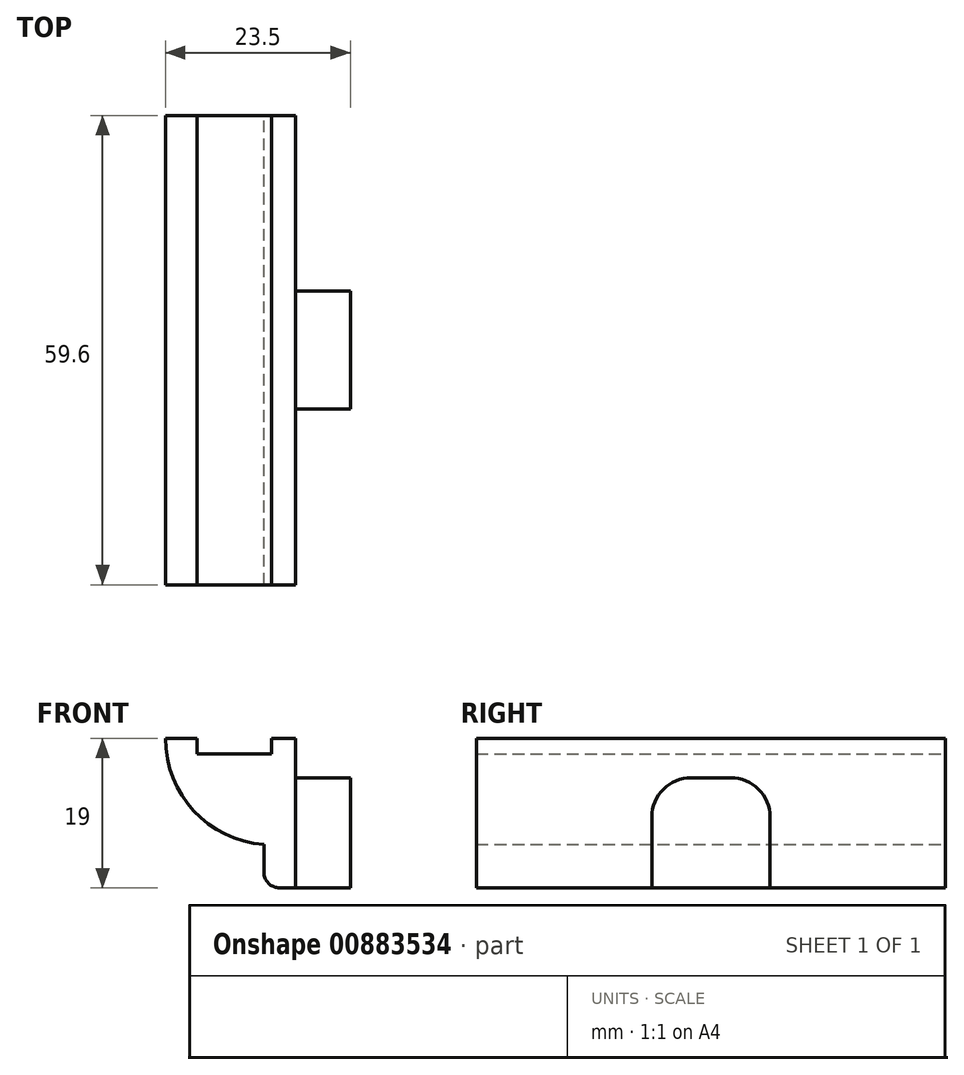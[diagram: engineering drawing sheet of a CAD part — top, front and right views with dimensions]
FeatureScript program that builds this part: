
annotation { "Feature Type Name" : "Feature", "Feature Type Description" : "" }
export const myFeature = defineFeature(function(context is Context, id is Id, definition is map)
    precondition{}
    {
        {
            var Q0;
            Q0=qCreatedBy(makeId("Front.planeOp"),FACE);
            var sketch = newSketch(context, id + "F0", { "sketchPlane" : qUnion([Q0])});
            skLineSegment(sketch, "E0.bottom", {"start": v(0, 9.5) * mm, "end": v(3, 9.5) * mm});
            skLineSegment(sketch, "E0.top", {"start": v(0, -9.5) * mm, "end": v(3, -9.5) * mm});
            skLineSegment(sketch, "E0.left", {"start": v(0, 9.5) * mm, "end": v(0, -9.5) * mm});
            skLineSegment(sketch, "E0.right", {"start": v(3, 9.5) * mm, "end": v(3, -9.5) * mm});
            skLineSegment(sketch, "E1", {"start": v(0, -9.5) * mm, "end": v(-1, -9.5) * mm});
            skLineSegment(sketch, "E2", {"start": v(-1, -9.5) * mm, "end": v(-1, -4) * mm});
            skLineSegment(sketch, "E3", {"start": v(0, 9.5) * mm, "end": v(0, 7.5) * mm, "construction": true});
            skLineSegment(sketch, "E4", {"start": v(0, 7.5) * mm, "end": v(-9.5, 7.5) * mm});
            skLineSegment(sketch, "E5", {"start": v(-9.5, 7.5) * mm, "end": v(-9.5, 9.5) * mm});
            skLineSegment(sketch, "E6", {"start": v(-9.5, 9.5) * mm, "end": v(-13.5, 9.5) * mm});
            skPoint(sketch, "E7.third.point", {"position": v(18.17, 13.18) * mm});
            skLineSegment(sketch, "E8", {"start": v(-13.5, 9.5) * mm, "end": v(-13.5, -4) * mm, "construction": true});
            skLineSegment(sketch, "E9", {"start": v(-13.5, -4) * mm, "end": v(-1, -4) * mm, "construction": true});
            skArc(sketch, "E10", {"start": v(-13.5, 9.5) * mm, "mid": v(-9.9, 0.3) * mm, "end": v(-1, -4) * mm});
            skSolve(sketch);
        }
        {
            var Q0;
            {var subQ1=sQuery(id+"F0.wireOp",EDGE,"E1");Q0=makeQuery(id+"F0.imprint","IMPRINT",FACE,{"disambiguationData":[TD([[makeQuery(id+"F0.imprint","IMPRINT",EDGE,{"derivedFrom":subQ1}),-1.0]])]});}
            var Q1;
            {var subQ3=sQuery(id+"F0.wireOp",EDGE,"E0.bottom");Q1=makeQuery(id+"F0.imprint","IMPRINT",FACE,{"disambiguationData":[TD([[makeQuery(id+"F0.imprint","IMPRINT",EDGE,{"derivedFrom":subQ3}),-1.0]])]});}
            extrude(context, id + "F1", {"entities" : qUnion([Q0, Q1]), "depth" : 59.6 * mm, "offsetDistance" : 25 * mm});
        }
        {
            var Q0;
            Q0=makeQuery(id+"F1.opExtrude","SWEPT_EDGE",EDGE,{"disambiguationData":[OSD([sQuery(id+"F0.wireOp",EDGE,"E1"),sQuery(id+"F0.wireOp",EDGE,"E2")])]});
            fillet(context, id + "F2", {"entities" : qUnion([Q0]), "radius" : 2 * mm, "tangentPropagation" : true, "allowEdgeOverflow" : false});
        }
        {
            var Q0;
            Q0=makeQuery(id+"F1.opExtrude","SWEPT_FACE",FACE,{"disambiguationData":[OSD([sQuery(id+"F0.wireOp",EDGE,"E0.right")])]});
            var sketch = newSketch(context, id + "F3", { "sketchPlane" : qUnion([Q0])});
            skLineSegment(sketch, "E11.bottom", {"start": v(-37.3, 4.5) * mm, "end": v(-22.3, 4.5) * mm});
            skLineSegment(sketch, "E11.top", {"start": v(-37.3, -9.5) * mm, "end": v(-22.3, -9.5) * mm});
            skLineSegment(sketch, "E11.left", {"start": v(-37.3, 4.5) * mm, "end": v(-37.3, -9.5) * mm});
            skLineSegment(sketch, "E11.right", {"start": v(-22.3, 4.5) * mm, "end": v(-22.3, -9.5) * mm});
            skSolve(sketch);
        }
        {
            var Q0;
            Q0=makeQuery(id+"F3.imprint","IMPRINT",FACE,{"disambiguationData":[TD([[makeQuery(id+"F3.imprint","IMPRINT",EDGE,{"derivedFrom":sQuery(id+"F3.wireOp",EDGE,"E11.bottom")}),-1.0]])]});
            extrude(context, id + "F4", {"entities" : qUnion([Q0]), "operationType" : NewBodyOperationType.ADD, "depth" : 7 * mm, "offsetDistance" : 25 * mm});
        }
        {
            var Q0;
            Q0=makeQuery(id+"F4.opExtrude","SWEPT_EDGE",EDGE,{"disambiguationData":[OSD([sQuery(id+"F3.wireOp",EDGE,"E11.bottom"),sQuery(id+"F3.wireOp",EDGE,"E11.left")])]});
            var Q1;
            Q1=makeQuery(id+"F4.opExtrude","SWEPT_EDGE",EDGE,{"disambiguationData":[OSD([sQuery(id+"F3.wireOp",EDGE,"E11.bottom"),sQuery(id+"F3.wireOp",EDGE,"E11.right")])]});
            fillet(context, id + "F5", {"entities" : qUnion([Q0, Q1]), "radius" : 5 * mm, "tangentPropagation" : true, "allowEdgeOverflow" : false});
        }
    });
